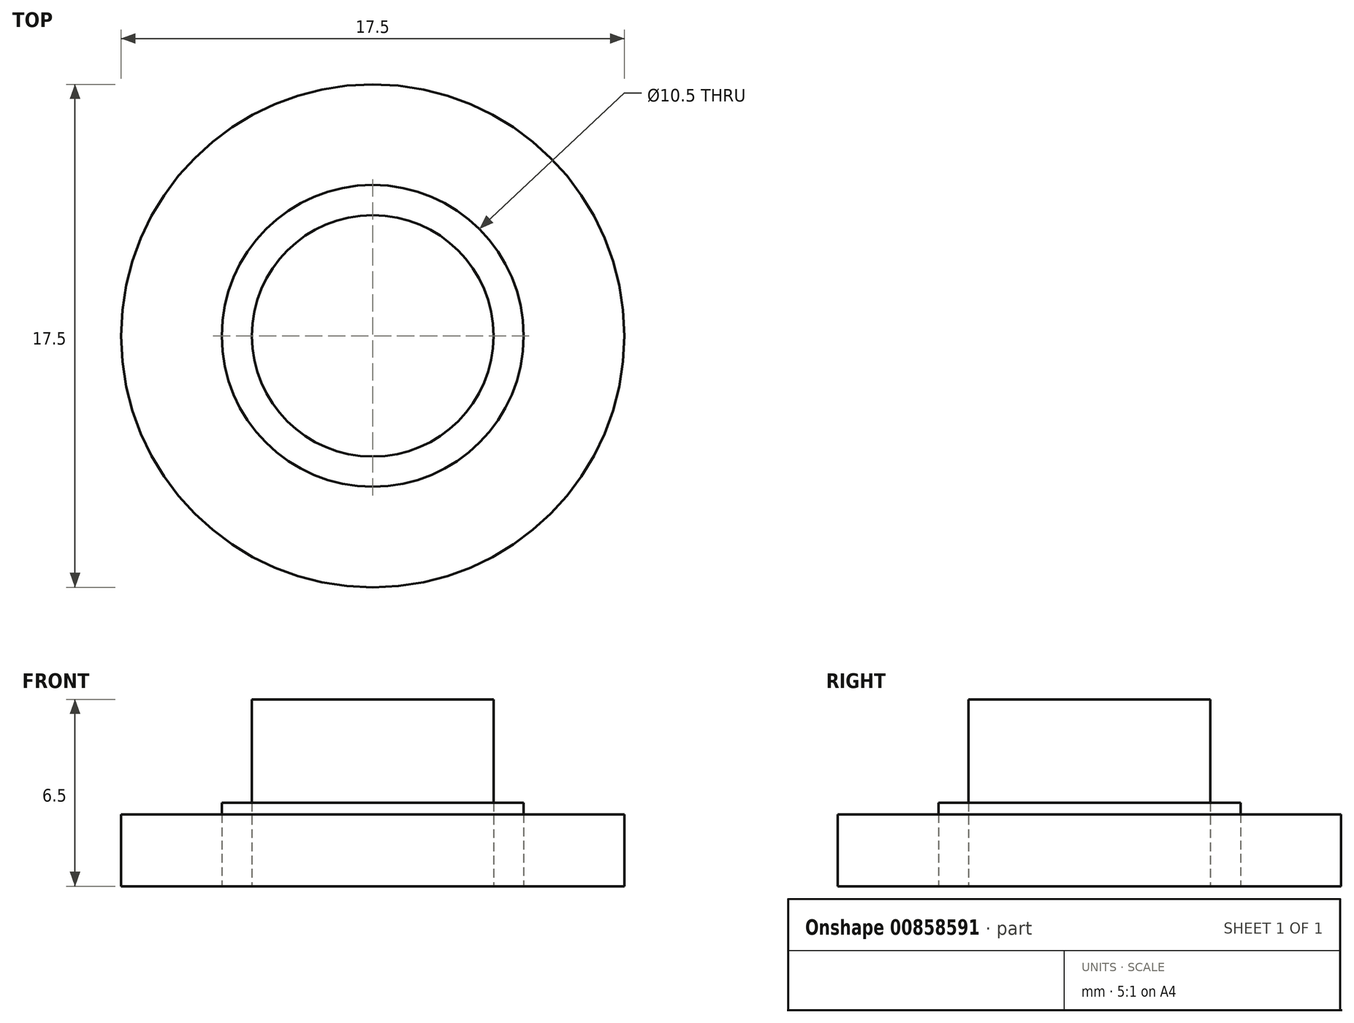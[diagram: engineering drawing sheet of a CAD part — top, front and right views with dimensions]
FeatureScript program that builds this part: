
annotation { "Feature Type Name" : "Feature", "Feature Type Description" : "" }
export const myFeature = defineFeature(function(context is Context, id is Id, definition is map)
    precondition{}
    {
        {
            var Q0;
            Q0=qCreatedBy(makeId("Top.planeOp"),FACE);
            var sketch = newSketch(context, id + "F0", { "sketchPlane" : qUnion([Q0])});
            skCircle(sketch, "E0", {"center": v(0, 0) * mm, "radius": 8.75 * mm});
            skCircle(sketch, "E1", {"center": v(0, 0) * mm, "radius": 4.2 * mm});
            skCircle(sketch, "E2", {"center": v(0, 0) * mm, "radius": 5.25 * mm});
            skSolve(sketch);
        }
        {
            var Q0;
            Q0 = qSketchRegion(id + "F0", true);
            extrude(context, id + "F1", {"entities" : qUnion([Q0]), "depth" : 2.5 * mm, "offsetDistance" : 25 * mm});
        }
        {
            var Q0;
            Q0=makeQuery(id+"F0.imprint","IMPRINT",FACE,{"disambiguationData":[TD([[makeQuery(id+"F0.imprint","IMPRINT",EDGE,{"derivedFrom":sQuery(id+"F0.wireOp",EDGE,"E1")}),1.0]])]});
            extrude(context, id + "F2", {"entities" : qUnion([Q0]), "operationType" : NewBodyOperationType.ADD, "depth" : 6.5 * mm, "offsetDistance" : 25 * mm});
        }
        {
            var Q0;
            Q0=makeQuery(id+"F0.imprint","IMPRINT",FACE,{"disambiguationData":[TD([[makeQuery(id+"F0.imprint","IMPRINT",EDGE,{"derivedFrom":sQuery(id+"F0.wireOp",EDGE,"E1")}),-1.0]])]});
            extrude(context, id + "F3", {"entities" : qUnion([Q0]), "depth" : 2.9 * mm, "offsetDistance" : 25 * mm});
        }
    });
